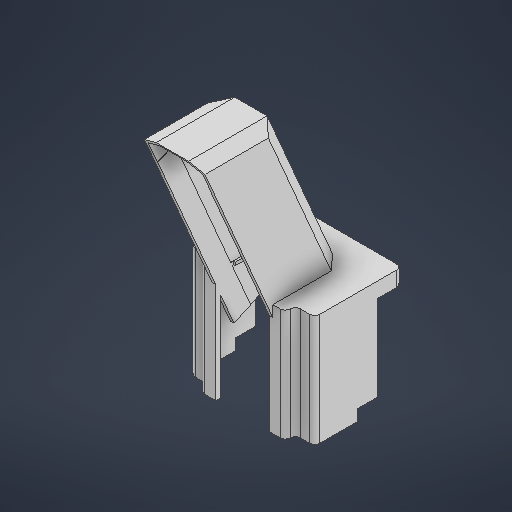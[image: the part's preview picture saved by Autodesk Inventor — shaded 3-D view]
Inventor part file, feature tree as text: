
AUTODESK INVENTOR PART (.ipt)
format: ipt  version: 2025 (Build 290162000, 162)  size: 439,296 bytes
history: native  units: in
note: dims shown in document units (in); Inventor stores cm internally (conversion verified against a paired STEP export)
features: extrude x8, sketch x7, chamfer x2, plane x2, fillet x1
ambient origin geometry x8: Origin, YZ Plane, XZ Plane, XY Plane, X Axis, Y Axis, Z Axis, Center Point
bodies: Solid1 (feature_tree)
feature tree (20):
  extrude  "Extrusion1"  Depth=0.1181in
  extrude  "Extrusion2"  Depth=0.0787in
  extrude  "Extrusion3"  Depth=1.9685in
  fillet  "Fillet1"  Radius=0.9843in
  chamfer  "Chamfer1"  Distance=0.4724in
  plane  "Work Plane1"
  extrude  "Extrusion4"  Depth=0.2165in
  chamfer  "Chamfer3"  Distance=0.1181in
  extrude  "Extrusion8"  Depth=0.1181in
  extrude  "Extrusion9"  Depth=0.1969in
  plane  "Work Plane5"
  sketch  "Sketch13"  dims[d19=0.1969in d20=0.2165in d22=0.1181in d23=0.1181in d27=0.1969in d28=0.1378in d29=0.0787in d30=45.0deg d31=0.0787in d32=0.0787in d33=1.9685in d34=0.5906in d36=2.126in d38=0.1575in d39=2.2835in d40=0.1378in d41=2.3622in d42=5.315in d43=2.1969in d44=0.0in d45=0.0in d47=0.1575in d53=0.5512in d54=0.0787in d55=45.0deg d57=0.1181in d65=0.315in d67=0.3937in d69=0.6201in d70=0.3937in d71=0.7579in d72=0.315in d73=0.1598in d76=0.0787in d77=0.0787in d78=0.7579in d79=0.7579in d80=0.9843in d85=0.6201in d86=0.7579in d90=3.7598in d91=0.0in d92=1.9685in d93=0.7874in d94=0.4331in d95=0.0in d117=1.378in d118=0.3937in d119=0.0in d120=0.3937in d121=0.0in d122=0.0197in d123=0.0344in]
  extrude  "Extrusion13"  Depth=0.1378in TaperAngle=45.0deg
  extrude  "Extrusion14"  Depth=0.0787in
  sketch  "Sketch1"  dims[d1=2.9577in d2=0.1181in]
  sketch  "Sketch2"  dims[d4=0.1181in d5=0.0in d6=0.0787in]
  sketch  "Sketch3"  dims[d8=4.2323in d9=0.0in d10=1.9685in d11=0.9843in]
  sketch  "Sketch4"  dims[d12=0.9449in]
  sketch  "Sketch9"  dims[d13=0.2165in]
  sketch  "Sketch10"  dims[d15=90.0deg d17=0.4724in d18=0.0in]
